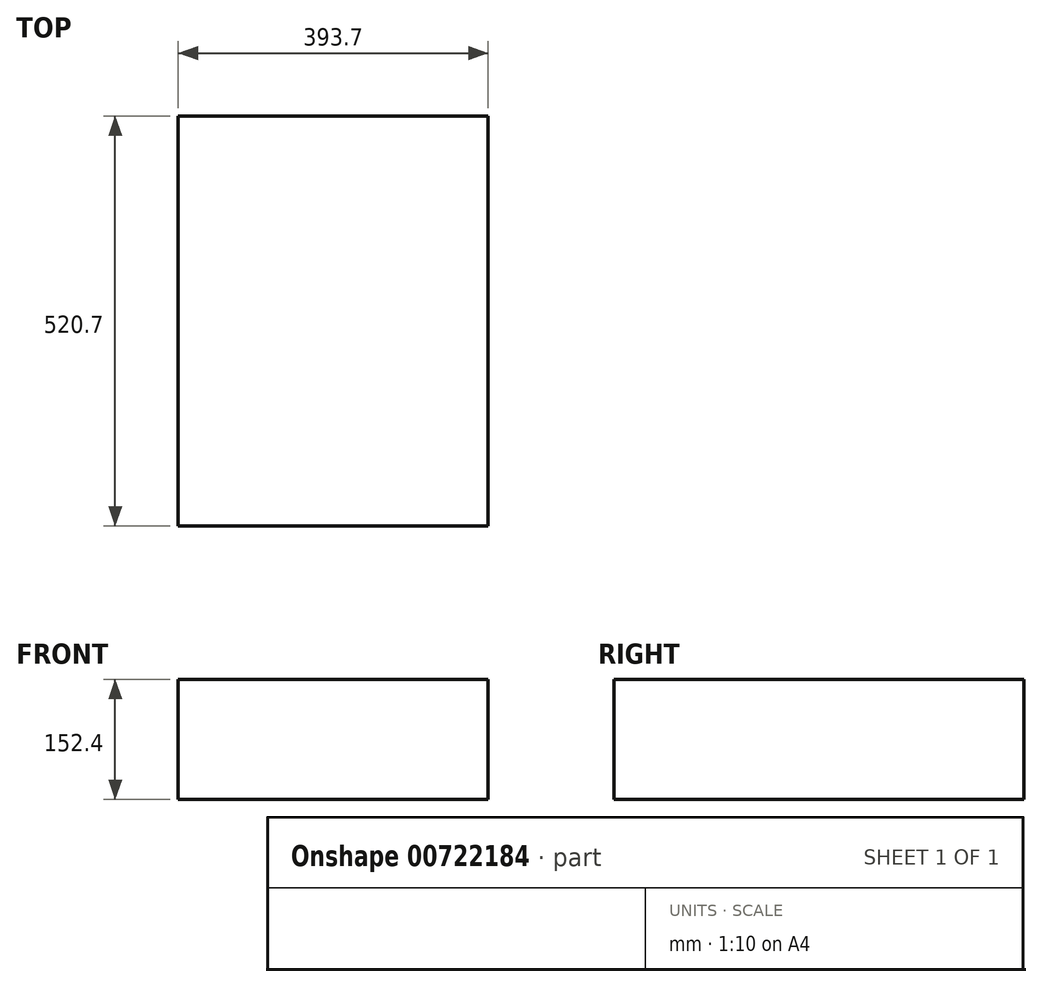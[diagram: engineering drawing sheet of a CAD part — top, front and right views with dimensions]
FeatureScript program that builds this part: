
annotation { "Feature Type Name" : "Feature", "Feature Type Description" : "" }
export const myFeature = defineFeature(function(context is Context, id is Id, definition is map)
    precondition{}
    {
        {
            var Q0;
            Q0=qCreatedBy(makeId("Top.planeOp"),FACE);
            var sketch = newSketch(context, id + "F0", { "sketchPlane" : qUnion([Q0])});
            skLineSegment(sketch, "E0.bottom", {"start": v(-196.85, 0) * mm, "end": v(196.85, 0) * mm});
            skLineSegment(sketch, "E0.top", {"start": v(-196.85, 520.7) * mm, "end": v(196.85, 520.7) * mm});
            skLineSegment(sketch, "E0.left", {"start": v(-196.85, 0) * mm, "end": v(-196.85, 520.7) * mm});
            skLineSegment(sketch, "E0.right", {"start": v(196.85, 0) * mm, "end": v(196.85, 520.7) * mm});
            skLineSegment(sketch, "E1", {"start": v(0, 0) * mm, "end": v(0, 397.98) * mm, "construction": true});
            skSolve(sketch);
        }
        {
            var Q0;
            Q0 = qSketchRegion(id + "F0", true);
            extrude(context, id + "F1", {"entities" : qUnion([Q0]), "depth" : 152.4 * mm, "offsetDistance" : 25.4 * mm});
        }
    });
